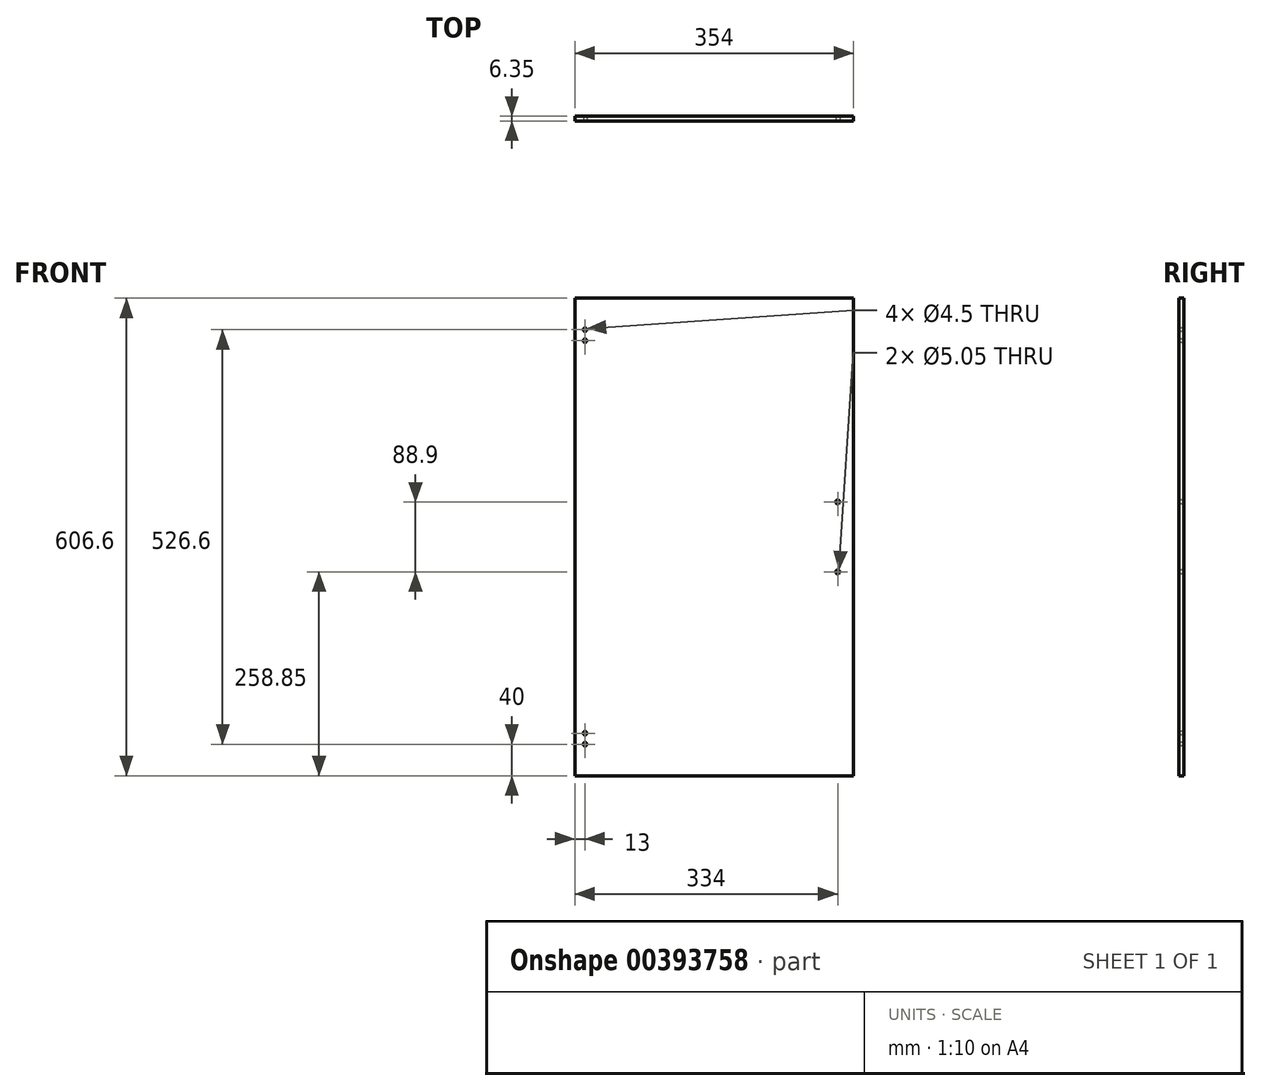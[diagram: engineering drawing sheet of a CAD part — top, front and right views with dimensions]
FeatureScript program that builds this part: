
annotation { "Feature Type Name" : "Feature", "Feature Type Description" : "" }
export const myFeature = defineFeature(function(context is Context, id is Id, definition is map)
    precondition{}
    {
        {
            var Q0;
            Q0=qCreatedBy(makeId("Front.planeOp"),FACE);
            var sketch = newSketch(context, id + "F0", { "sketchPlane" : qUnion([Q0])});
            skLineSegment(sketch, "E0.bottom", {"start": v(0, 303.3) * mm, "end": v(354, 303.3) * mm});
            skLineSegment(sketch, "E0.top", {"start": v(0, -303.3) * mm, "end": v(354, -303.3) * mm});
            skLineSegment(sketch, "E0.left", {"start": v(0, 303.3) * mm, "end": v(0, -303.3) * mm});
            skLineSegment(sketch, "E0.right", {"start": v(354, 303.3) * mm, "end": v(354, -303.3) * mm});
            skPoint(sketch, "E1", {"position": v(13, 263.3) * mm});
            skPoint(sketch, "E2", {"position": v(13, 249.3) * mm});
            skLineSegment(sketch, "E3", {"start": v(13, 263.3) * mm, "end": v(13, 249.3) * mm, "construction": true});
            skLineSegment(sketch, "E4", {"start": v(13, 249.3) * mm, "end": v(0, 249.3) * mm, "construction": true});
            skLineSegment(sketch, "E5.MirrorCS", {"start": v(13, -263.3) * mm, "end": v(13, -249.3) * mm, "construction": true});
            skLineSegment(sketch, "E6.MirrorCS", {"start": v(13, -249.3) * mm, "end": v(0, -249.3) * mm, "construction": true});
            skPoint(sketch, "E7.MirrorP", {"position": v(13, -249.3) * mm});
            skPoint(sketch, "E8.MirrorP", {"position": v(13, -263.3) * mm});
            skLineSegment(sketch, "E9", {"start": v(354, 0) * mm, "end": v(0, 0) * mm, "construction": true});
            skPoint(sketch, "E10", {"position": v(334, 44.45) * mm});
            skPoint(sketch, "E11", {"position": v(334, -44.45) * mm});
            skLineSegment(sketch, "E12", {"start": v(334, 44.45) * mm, "end": v(334, -44.45) * mm, "construction": true});
            skSolve(sketch);
        }
        {
            var Q0;
            Q0 = qSketchRegion(id + "F0", true);
            extrude(context, id + "F1", {"entities" : qUnion([Q0]), "oppositeDirection" : true, "depth" : 6.35 * mm});
        }
        {
            var Q0;
            Q0=sQuery(id+"F0.wireOp",VERTEX,"E1");
            var Q1;
            Q1=sQuery(id+"F0.wireOp",VERTEX,"E2");
            var Q2;
            Q2=sQuery(id+"F0.wireOp",VERTEX,"E7.MirrorP");
            var Q3;
            Q3=sQuery(id+"F0.wireOp",VERTEX,"E8.MirrorP");
            var Q4;
            Q4=makeQuery(id+"F1.opExtrude","SWEPT_BODY",BODY,{"disambiguationData":[OSD([sQuery(id+"F0.wireOp",EDGE,"E0.bottom"),sQuery(id+"F0.wireOp",EDGE,"E0.top"),sQuery(id+"F0.wireOp",EDGE,"E0.left"),sQuery(id+"F0.wireOp",EDGE,"E0.right")])]});
            hole(context, id + "F2", {"style" : HoleStyle.SIMPLE, "endStyle" : HoleEndStyle.THROUGH, "standardTappedOrClearance" : lookupTablePath({ "standard" : "ISO", "size" : "4.5", "type" : "Drilled" }), "standardBlindInLast" : lookupTablePath({ "standard" : "ISO", "size" : "4.5", "type" : "Drilled" }), "holeDiameter" : 4.5 * mm, "tappedDepth" : 12 * mm, "tapClearance" : 3, "startFromSketch" : true, "locations" : qUnion([Q0, Q1, Q2, Q3]), "scope" : qUnion([Q4])});
        }
        {
            var Q0;
            Q0=sQuery(id+"F0.wireOp",VERTEX,"E10");
            var Q1;
            Q1=sQuery(id+"F0.wireOp",VERTEX,"E11");
            var Q2;
            Q2=makeQuery(id+"F1.opExtrude","SWEPT_BODY",BODY,{"disambiguationData":[OSD([sQuery(id+"F0.wireOp",EDGE,"E0.bottom"),sQuery(id+"F0.wireOp",EDGE,"E0.top"),sQuery(id+"F0.wireOp",EDGE,"E0.left"),sQuery(id+"F0.wireOp",EDGE,"E0.right")])]});
            hole(context, id + "F3", {"style" : HoleStyle.SIMPLE, "endStyle" : HoleEndStyle.THROUGH, "standardTappedOrClearance" : lookupTablePath({ "standard" : "ANSI", "size" : "#8 (0.2)", "type" : "Drilled" }), "standardBlindInLast" : lookupTablePath({ "standard" : "ANSI", "size" : "#8", "type" : "Drilled" }), "holeDiameter" : 5.05 * mm, "tappedDepth" : 12 * mm, "tapClearance" : 3, "startFromSketch" : true, "locations" : qUnion([Q0, Q1]), "scope" : qUnion([Q2])});
        }
    });
